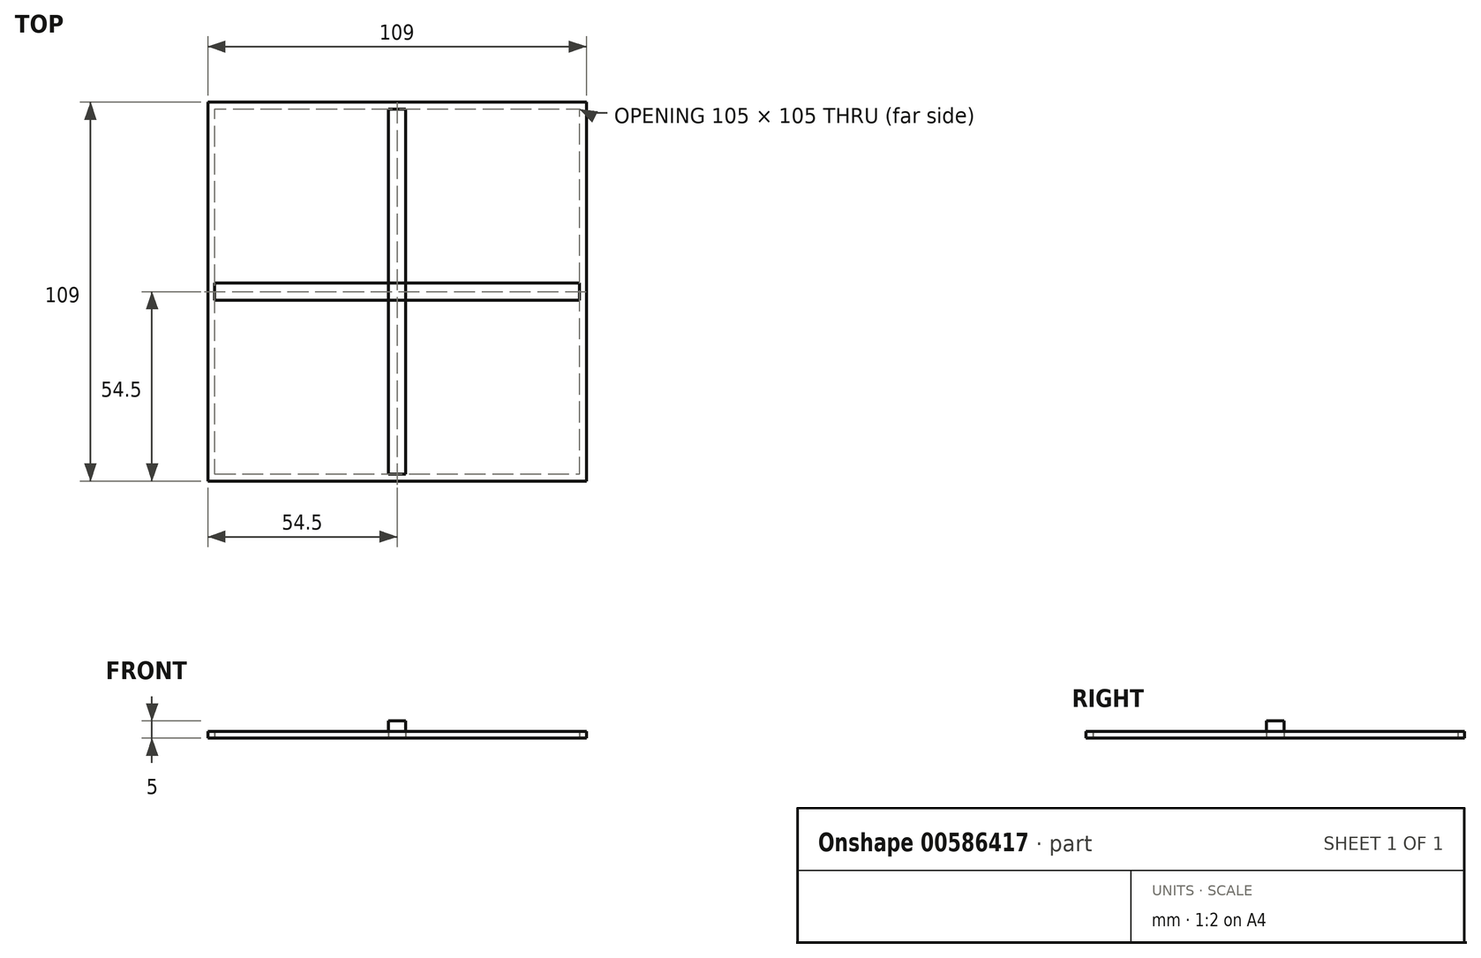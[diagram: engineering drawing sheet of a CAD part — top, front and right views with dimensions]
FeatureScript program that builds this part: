
annotation { "Feature Type Name" : "Feature", "Feature Type Description" : "" }
export const myFeature = defineFeature(function(context is Context, id is Id, definition is map)
    precondition{}
    {
        {
            var Q0;
            Q0=qCreatedBy(makeId("Top.planeOp"),FACE);
            var sketch = newSketch(context, id + "F0", { "sketchPlane" : qUnion([Q0])});
            skLineSegment(sketch, "E0.bottom", {"start": v(-52.5, -52.5) * mm, "end": v(52.5, -52.5) * mm});
            skLineSegment(sketch, "E0.top", {"start": v(-52.5, 52.5) * mm, "end": v(52.5, 52.5) * mm});
            skLineSegment(sketch, "E0.left", {"start": v(-52.5, -52.5) * mm, "end": v(-52.5, 52.5) * mm});
            skLineSegment(sketch, "E0.right", {"start": v(52.5, -52.5) * mm, "end": v(52.5, 52.5) * mm});
            skPoint(sketch, "E0.middle", {"position": v(0, 0) * mm});
            skLineSegment(sketch, "E1.bottom", {"start": v(-52.5, -2.5) * mm, "end": v(52.5, -2.5) * mm});
            skLineSegment(sketch, "E1.top", {"start": v(-52.5, 2.5) * mm, "end": v(52.5, 2.5) * mm});
            skLineSegment(sketch, "E1.left", {"start": v(-52.5, -2.5) * mm, "end": v(-52.5, 2.5) * mm});
            skLineSegment(sketch, "E1.right", {"start": v(52.5, -2.5) * mm, "end": v(52.5, 2.5) * mm});
            skLineSegment(sketch, "E2.bottom", {"start": v(2.5, 52.5) * mm, "end": v(-2.5, 52.5) * mm});
            skLineSegment(sketch, "E2.top", {"start": v(2.5, -52.5) * mm, "end": v(-2.5, -52.5) * mm});
            skLineSegment(sketch, "E2.left", {"start": v(2.5, 52.5) * mm, "end": v(2.5, -52.5) * mm});
            skLineSegment(sketch, "E2.right", {"start": v(-2.5, 52.5) * mm, "end": v(-2.5, -52.5) * mm});
            skLineSegment(sketch, "E3.0", {"start": v(-54.5, 54.5) * mm, "end": v(54.5, 54.5) * mm});
            skLineSegment(sketch, "E3.1", {"start": v(-54.5, -54.5) * mm, "end": v(-54.5, 54.5) * mm});
            skLineSegment(sketch, "E3.2", {"start": v(-54.5, -54.5) * mm, "end": v(54.5, -54.5) * mm});
            skLineSegment(sketch, "E3.3", {"start": v(54.5, -54.5) * mm, "end": v(54.5, 54.5) * mm});
            skSolve(sketch);
        }
        {
            var Q0;
            Q0 = qSketchRegion(id + "F0", true);
            var Q1;
            {var subQ0=sQuery(id+"F0.wireOp",EDGE,"E2.right");var subQ1=sQuery(id+"F0.wireOp",EDGE,"E1.bottom");var subQ2=makeQuery(id+"F0.imprint","INTERSECT",VERTEX,{"derivedFrom":[subQ1,subQ0]});Q1=makeQuery(id+"F0.imprint","IMPRINT",FACE,{"disambiguationData":[TD([[makeQuery(id+"F0.imprint","IMPRINT",EDGE,{"disambiguationData":[TD([[subQ2,-1.0]])],"derivedFrom":subQ1}),1.0]])]});}
            var Q2;
            {var subQ0=sQuery(id+"F0.wireOp",EDGE,"E0.left");var subQ1=sQuery(id+"F0.wireOp",EDGE,"E0.top");var subQ2=makeQuery(id+"F0.imprint","INTERSECT",VERTEX,{"derivedFrom":[subQ1,subQ0]});Q2=makeQuery(id+"F0.imprint","IMPRINT",FACE,{"disambiguationData":[TD([[makeQuery(id+"F0.imprint","IMPRINT",EDGE,{"disambiguationData":[TD([[subQ2,-1.0]])],"derivedFrom":subQ1}),-1.0]])]});}
            var Q3;
            {var subQ0=sQuery(id+"F0.wireOp",EDGE,"E0.left");var subQ1=sQuery(id+"F0.wireOp",EDGE,"E0.bottom");var subQ2=makeQuery(id+"F0.imprint","INTERSECT",VERTEX,{"derivedFrom":[subQ1,subQ0]});Q3=makeQuery(id+"F0.imprint","IMPRINT",FACE,{"disambiguationData":[TD([[makeQuery(id+"F0.imprint","IMPRINT",EDGE,{"disambiguationData":[TD([[subQ2,-1.0]])],"derivedFrom":subQ1}),1.0]])]});}
            var Q4;
            {var subQ0=sQuery(id+"F0.wireOp",EDGE,"E0.right");var subQ1=sQuery(id+"F0.wireOp",EDGE,"E0.bottom");var subQ2=makeQuery(id+"F0.imprint","INTERSECT",VERTEX,{"derivedFrom":[subQ1,subQ0]});Q4=makeQuery(id+"F0.imprint","IMPRINT",FACE,{"disambiguationData":[TD([[makeQuery(id+"F0.imprint","IMPRINT",EDGE,{"disambiguationData":[TD([[subQ2,1.0]])],"derivedFrom":subQ1}),1.0]])]});}
            var Q5;
            {var subQ0=sQuery(id+"F0.wireOp",EDGE,"E0.right");var subQ1=sQuery(id+"F0.wireOp",EDGE,"E0.top");var subQ2=makeQuery(id+"F0.imprint","INTERSECT",VERTEX,{"derivedFrom":[subQ1,subQ0]});Q5=makeQuery(id+"F0.imprint","IMPRINT",FACE,{"disambiguationData":[TD([[makeQuery(id+"F0.imprint","IMPRINT",EDGE,{"disambiguationData":[TD([[subQ2,1.0]])],"derivedFrom":subQ1}),-1.0]])]});}
            var Q6;
            {var subQ5=sQuery(id+"F0.wireOp",EDGE,"E2.bottom");Q6=makeQuery(id+"F0.imprint","IMPRINT",FACE,{"disambiguationData":[TD([[makeQuery(id+"F0.imprint","IMPRINT",EDGE,{"derivedFrom":subQ5}),1.0]])]});}
            var Q7;
            {var subQ0=sQuery(id+"F0.wireOp",EDGE,"E1.right");Q7=makeQuery(id+"F0.imprint","IMPRINT",FACE,{"disambiguationData":[TD([[makeQuery(id+"F0.imprint","IMPRINT",EDGE,{"derivedFrom":subQ0}),1.0]])]});}
            var Q8;
            {var subQ5=sQuery(id+"F0.wireOp",EDGE,"E2.top");Q8=makeQuery(id+"F0.imprint","IMPRINT",FACE,{"disambiguationData":[TD([[makeQuery(id+"F0.imprint","IMPRINT",EDGE,{"derivedFrom":subQ5}),-1.0]])]});}
            var Q9;
            {var subQ0=sQuery(id+"F0.wireOp",EDGE,"E1.left");Q9=makeQuery(id+"F0.imprint","IMPRINT",FACE,{"disambiguationData":[TD([[makeQuery(id+"F0.imprint","IMPRINT",EDGE,{"derivedFrom":subQ0}),-1.0]])]});}
            extrude(context, id + "F1", {"entities" : qUnion([Q0, Q1, Q2, Q3, Q4, Q5, Q6, Q7, Q8, Q9]), "depth" : 2 * mm, "offsetDistance" : 25 * mm});
        }
        {
            var Q0;
            {var subQ5=sQuery(id+"F0.wireOp",EDGE,"E2.top");Q0=makeQuery(id+"F0.imprint","IMPRINT",FACE,{"disambiguationData":[TD([[makeQuery(id+"F0.imprint","IMPRINT",EDGE,{"derivedFrom":subQ5}),-1.0]])]});}
            var Q1;
            {var subQ0=sQuery(id+"F0.wireOp",EDGE,"E1.right");Q1=makeQuery(id+"F0.imprint","IMPRINT",FACE,{"disambiguationData":[TD([[makeQuery(id+"F0.imprint","IMPRINT",EDGE,{"derivedFrom":subQ0}),1.0]])]});}
            var Q2;
            {var subQ0=sQuery(id+"F0.wireOp",EDGE,"E2.right");var subQ1=sQuery(id+"F0.wireOp",EDGE,"E1.bottom");var subQ2=makeQuery(id+"F0.imprint","INTERSECT",VERTEX,{"derivedFrom":[subQ1,subQ0]});Q2=makeQuery(id+"F0.imprint","IMPRINT",FACE,{"disambiguationData":[TD([[makeQuery(id+"F0.imprint","IMPRINT",EDGE,{"disambiguationData":[TD([[subQ2,-1.0]])],"derivedFrom":subQ1}),1.0]])]});}
            var Q3;
            {var subQ0=sQuery(id+"F0.wireOp",EDGE,"E1.left");Q3=makeQuery(id+"F0.imprint","IMPRINT",FACE,{"disambiguationData":[TD([[makeQuery(id+"F0.imprint","IMPRINT",EDGE,{"derivedFrom":subQ0}),-1.0]])]});}
            var Q4;
            {var subQ5=sQuery(id+"F0.wireOp",EDGE,"E2.bottom");Q4=makeQuery(id+"F0.imprint","IMPRINT",FACE,{"disambiguationData":[TD([[makeQuery(id+"F0.imprint","IMPRINT",EDGE,{"derivedFrom":subQ5}),1.0]])]});}
            var Q5;
            {var subQ10=sQuery(id+"F0.wireOp",EDGE,"E1.left");Q5=makeQuery(id+"F0.imprint","IMPRINT",FACE,{"disambiguationData":[TD([[makeQuery(id+"F0.imprint","IMPRINT",EDGE,{"derivedFrom":subQ10}),1.0]])]});}
            extrude(context, id + "F2", {"entities" : qUnion([Q0, Q1, Q2, Q3, Q4, Q5]), "operationType" : NewBodyOperationType.ADD, "depth" : 5 * mm, "offsetDistance" : 25 * mm});
        }
    });
